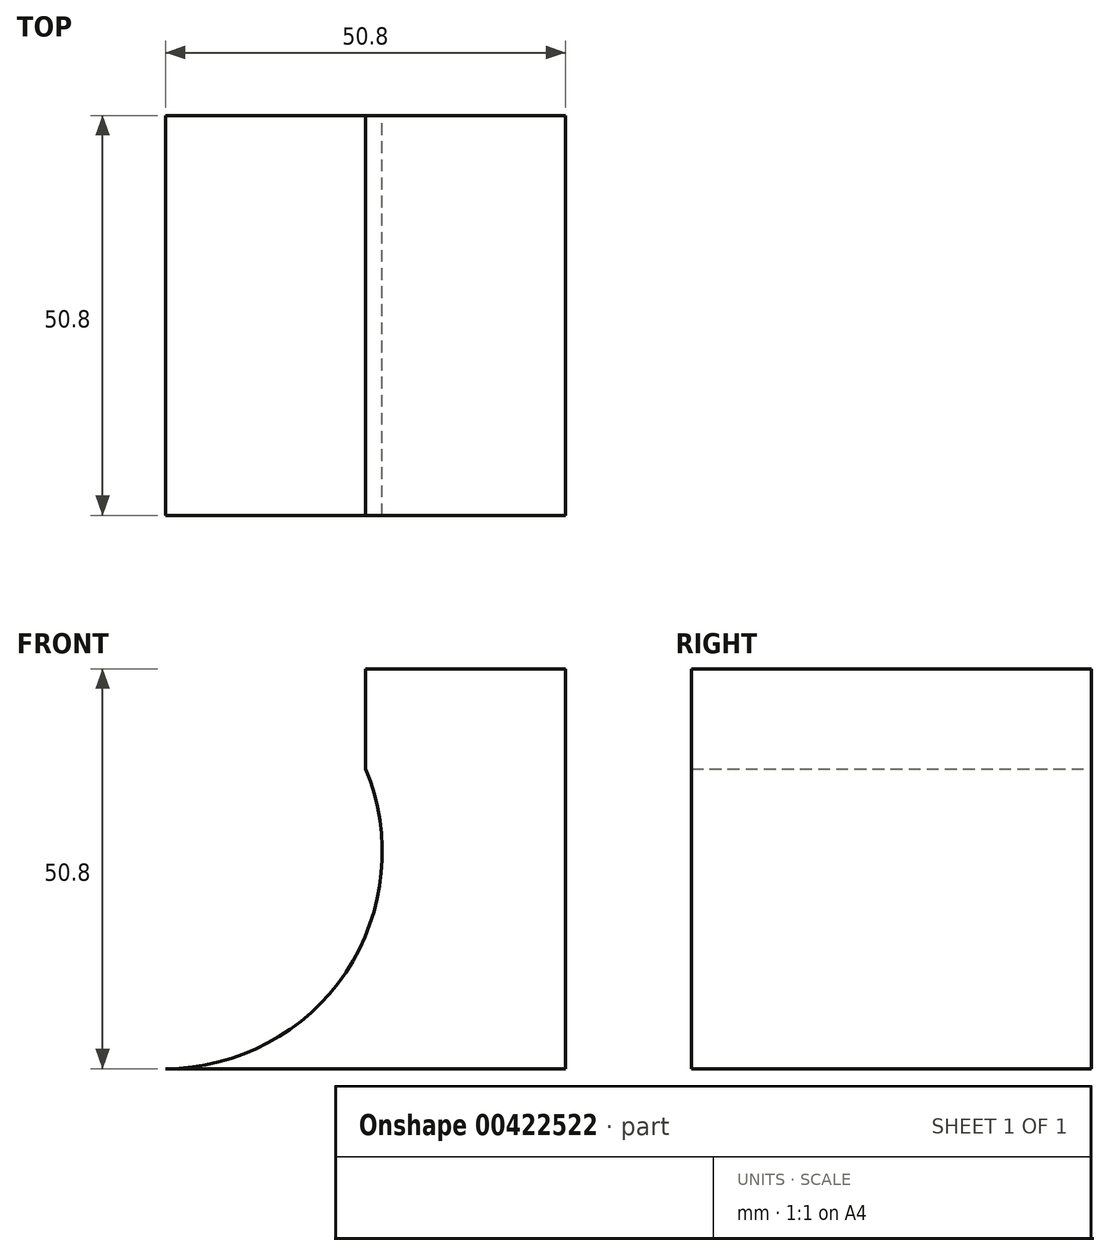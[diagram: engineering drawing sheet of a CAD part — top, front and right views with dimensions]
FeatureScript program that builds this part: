
annotation { "Feature Type Name" : "Feature", "Feature Type Description" : "" }
export const myFeature = defineFeature(function(context is Context, id is Id, definition is map)
    precondition{}
    {
        {
            var Q0;
            Q0=qCreatedBy(makeId("Front.planeOp"),FACE);
            var sketch = newSketch(context, id + "F0", { "sketchPlane" : qUnion([Q0])});
            skLineSegment(sketch, "E0", {"start": v(0, 0) * mm, "end": v(0, 50.8) * mm});
            skLineSegment(sketch, "E1", {"start": v(0, 0) * mm, "end": v(-25.4, 0) * mm});
            skLineSegment(sketch, "E2", {"start": v(-25.4, 0) * mm, "end": v(-50.8, 0) * mm});
            skLineSegment(sketch, "E3", {"start": v(0, 50.8) * mm, "end": v(-25.4, 50.8) * mm});
            skLineSegment(sketch, "E4", {"start": v(-25.4, 50.8) * mm, "end": v(-25.4, 38.1) * mm});
            skArc(sketch, "E5", {"start": v(-50.8, 0) * mm, "mid": v(-27.9, 12.25) * mm, "end": v(-25.4, 38.1) * mm});
            skSolve(sketch);
        }
        {
            var Q0;
            Q0 = qSketchRegion(id + "F0", true);
            extrude(context, id + "F1", {"entities" : qUnion([Q0]), "depth" : 50.8 * mm});
        }
    });
